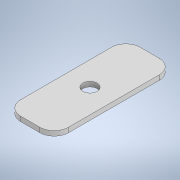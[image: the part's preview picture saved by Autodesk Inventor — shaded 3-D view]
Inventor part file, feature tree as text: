
AUTODESK INVENTOR PART (.ipt)
format: ipt  version: 2021 (Build 250183000, 183)  size: 117,760 bytes
history: native  units: mm
features: other x3, sketch x2, hole x1
ambient origin geometry x8: Origin, YZ Plane, XZ Plane, XY Plane, X Axis, Y Axis, Z Axis, Center Point
bodies: Body1 (feature_tree)
feature tree (6):
  other  "實體1"
  other  "轉角外圓角1"
  hole  "孔2"  [1 undecoded]
  sketch  "草圖1"
  other  "平板1"
  sketch  "草圖4"
note: 1 required parameter value undecoded (feature->parameter linkage not recoverable at this tier; creation-order binding heuristic only, values carry confidence <= 0.55)
